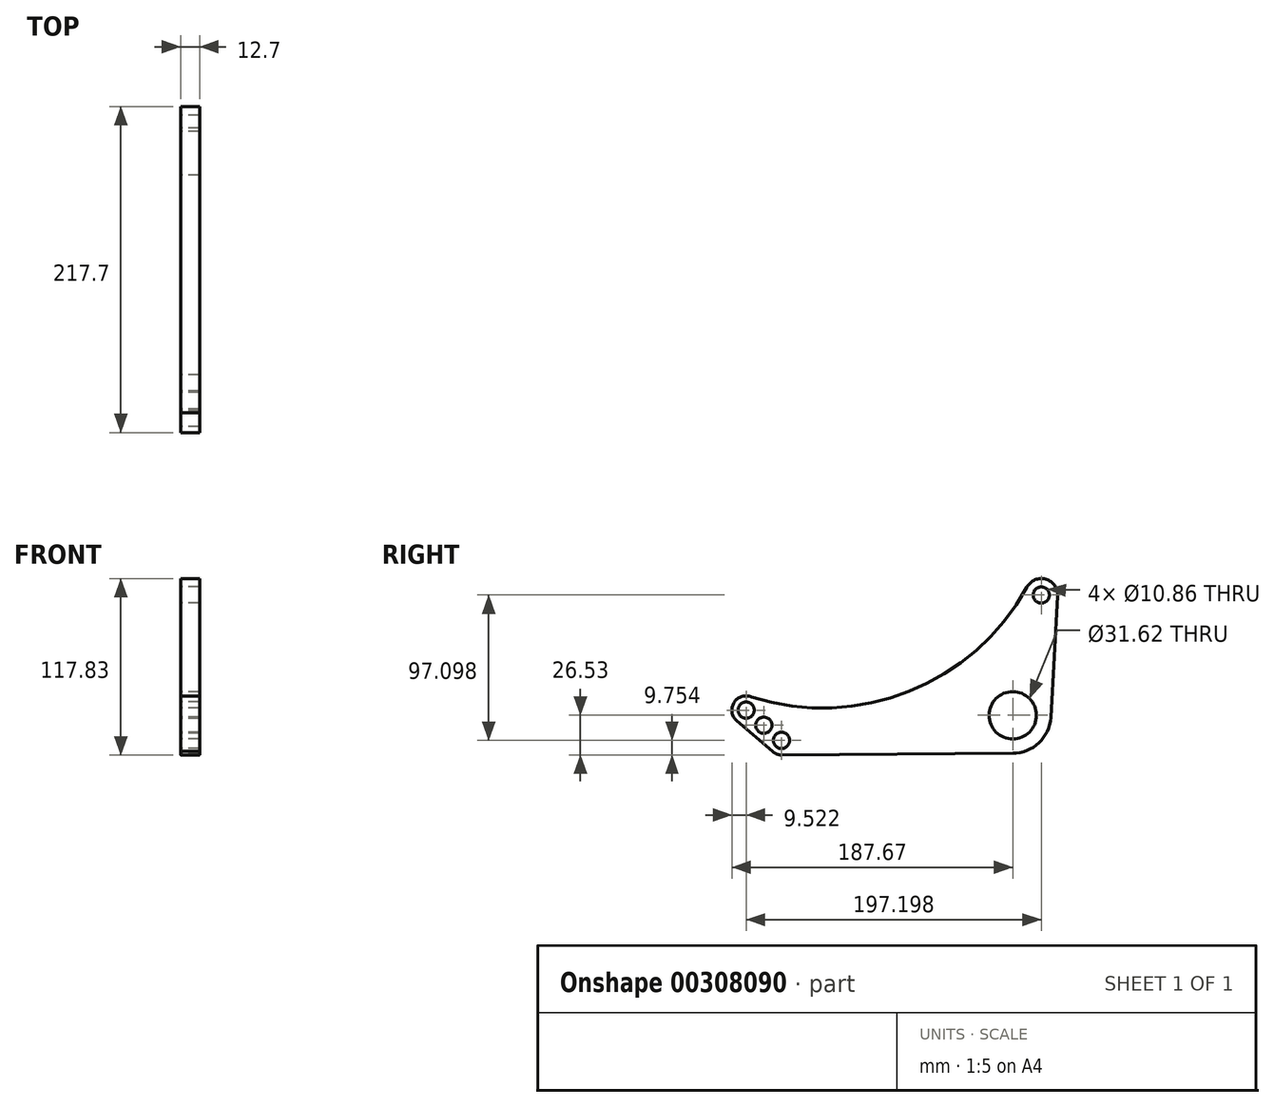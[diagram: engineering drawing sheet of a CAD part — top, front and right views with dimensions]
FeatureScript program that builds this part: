
annotation { "Feature Type Name" : "Feature", "Feature Type Description" : "" }
export const myFeature = defineFeature(function(context is Context, id is Id, definition is map)
    precondition{}
    {
        {
            var Q0;
            Q0=qCreatedBy(makeId("Right.planeOp"),FACE);
            var sketch = newSketch(context, id + "F0", { "sketchPlane" : qUnion([Q0])});
            skCircle(sketch, "E0", {"center": v(0, 0) * mm, "radius": 15.81 * mm});
            skArc(sketch, "E1", {"start": v(0, -25.4) * mm, "mid": v(17.44, -18.47) * mm, "end": v(25.36, -1.45) * mm});
            skCircle(sketch, "E2", {"center": v(-178.15, 3.44) * mm, "radius": 5.43 * mm});
            skCircle(sketch, "E3", {"center": v(19.05, 80.32) * mm, "radius": 5.43 * mm});
            skArc(sketch, "E4", {"start": v(30.01, 79.7) * mm, "mid": v(22.08, 90.87) * mm, "end": v(9.42, 85.6) * mm});
            skLineSegment(sketch, "E5", {"start": v(30.01, 79.7) * mm, "end": v(25.36, -1.45) * mm});
            skArc(sketch, "E6", {"start": v(-174.65, 12.28) * mm, "mid": v(-69.43, 15.85) * mm, "end": v(9.42, 85.6) * mm});
            skArc(sketch, "E7", {"start": v(-174.45, 12.22) * mm, "mid": v(-186.25, 8.45) * mm, "end": v(-184.34, -3.8) * mm});
            skArc(sketch, "E8", {"start": v(-160.69, -24.02) * mm, "mid": v(-157.84, -25.9) * mm, "end": v(-154.49, -26.53) * mm});
            skLineSegment(sketch, "E9", {"start": v(0, -25.4) * mm, "end": v(-154.74, -26.54) * mm});
            skLineSegment(sketch, "E10", {"start": v(-160.69, -24.02) * mm, "end": v(-184.34, -3.8) * mm});
            skCircle(sketch, "E11", {"center": v(-154.5, -16.78) * mm, "radius": 5.43 * mm});
            skCircle(sketch, "E12", {"center": v(-166.32, -6.67) * mm, "radius": 5.43 * mm});
            skSolve(sketch);
        }
        {
            var Q0;
            Q0=makeQuery(id+"F0.imprint","IMPRINT",FACE,{"disambiguationData":[TD([[makeQuery(id+"F0.imprint","IMPRINT",EDGE,{"derivedFrom":sQuery(id+"F0.wireOp",EDGE,"E0")}),-1.0]])]});
            extrude(context, id + "F1", {"entities" : qUnion([Q0]), "depth" : 12.7 * mm, "offsetDistance" : 25.4 * mm});
        }
    });
